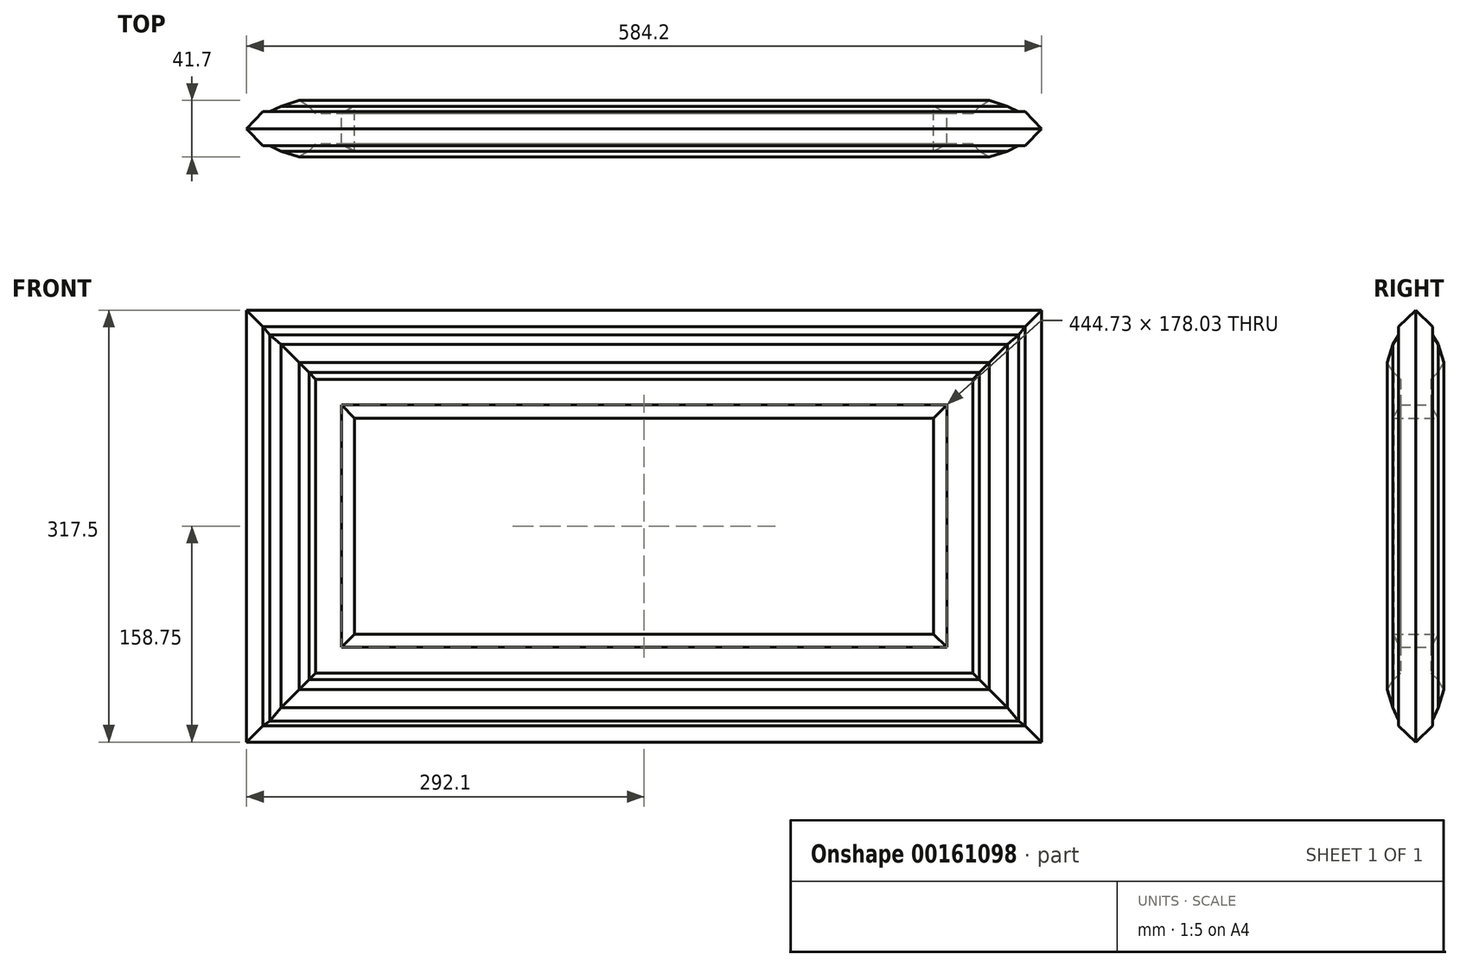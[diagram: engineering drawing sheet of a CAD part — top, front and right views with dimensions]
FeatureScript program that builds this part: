
annotation { "Feature Type Name" : "Feature", "Feature Type Description" : "" }
export const myFeature = defineFeature(function(context is Context, id is Id, definition is map)
    precondition{}
    {
        {
            var Q0;
            Q0=qCreatedBy(makeId("Front.planeOp"),FACE);
            var sketch = newSketch(context, id + "F0", { "sketchPlane" : qUnion([Q0])});
            skLineSegment(sketch, "E0.bottom", {"start": v(212.75, 79.4) * mm, "end": v(-212.75, 79.4) * mm});
            skLineSegment(sketch, "E0.top", {"start": v(212.75, -79.4) * mm, "end": v(-212.75, -79.4) * mm});
            skLineSegment(sketch, "E0.left", {"start": v(212.75, 79.4) * mm, "end": v(212.75, -79.4) * mm});
            skLineSegment(sketch, "E0.right", {"start": v(-212.75, 79.4) * mm, "end": v(-212.75, -79.4) * mm});
            skPoint(sketch, "E0.middle", {"position": v(0, 0) * mm});
            skSolve(sketch);
        }
        {
            var Q0;
            Q0 = qSketchRegion(id + "F0", true);
            extrude(context, id + "F1", {"entities" : qUnion([Q0]), "depth" : 16.67 * mm, "hasSecondDirection" : true, "secondDirectionOppositeDirection" : true, "secondDirectionDepth" : 16.67 * mm});
        }
        {
            var Q0;
            Q0=qCreatedBy(makeId("Front.planeOp"),FACE);
            var sketch = newSketch(context, id + "F2", { "sketchPlane" : qUnion([Q0])});
            skLineSegment(sketch, "E1.bottom", {"start": v(222.36, 89.01) * mm, "end": v(-222.36, 89.01) * mm});
            skLineSegment(sketch, "E1.top", {"start": v(222.36, -89.01) * mm, "end": v(-222.36, -89.01) * mm});
            skLineSegment(sketch, "E1.left", {"start": v(222.36, 89.01) * mm, "end": v(222.36, -89.01) * mm});
            skLineSegment(sketch, "E1.right", {"start": v(-222.36, 89.01) * mm, "end": v(-222.36, -89.01) * mm});
            skPoint(sketch, "E1.middle", {"position": v(0, 0) * mm});
            skLineSegment(sketch, "E2.bottom", {"start": v(241.38, 108.03) * mm, "end": v(-241.38, 108.03) * mm});
            skLineSegment(sketch, "E2.top", {"start": v(241.38, -108.03) * mm, "end": v(-241.38, -108.03) * mm});
            skLineSegment(sketch, "E2.left", {"start": v(241.38, 108.03) * mm, "end": v(241.38, -108.03) * mm});
            skLineSegment(sketch, "E2.right", {"start": v(-241.38, 108.03) * mm, "end": v(-241.38, -108.03) * mm});
            skSolve(sketch);
        }
        {
            var Q0;
            Q0 = qSketchRegion(id + "F2", true);
            extrude(context, id + "F3", {"entities" : qUnion([Q0]), "depth" : 11.13 * mm, "hasSecondDirection" : true, "secondDirectionOppositeDirection" : true, "secondDirectionDepth" : 11.13 * mm});
        }
        {
            var Q0;
            Q0=makeQuery(id+"F1.opExtrude","SWEPT_FACE",FACE,{"disambiguationData":[OSD([sQuery(id+"F0.wireOp",EDGE,"E0.right")])]});
            var Q1;
            Q1=makeQuery(id+"F3.opExtrude","SWEPT_FACE",FACE,{"disambiguationData":[OSD([sQuery(id+"F2.wireOp",EDGE,"E1.right")])]});
            loft(context, id + "F4", {"sheetProfilesArray" : [{ "sheetProfileEntities" : qUnion([Q0]) }, { "sheetProfileEntities" : qUnion([Q1]) }]});
        }
        {
            var Q0;
            Q0=makeQuery(id+"F1.opExtrude","SWEPT_FACE",FACE,{"disambiguationData":[OSD([sQuery(id+"F0.wireOp",EDGE,"E0.bottom")])]});
            var Q1;
            Q1=makeQuery(id+"F3.opExtrude","SWEPT_FACE",FACE,{"disambiguationData":[OSD([sQuery(id+"F2.wireOp",EDGE,"E1.bottom")])]});
            loft(context, id + "F5", {"sheetProfilesArray" : [{ "sheetProfileEntities" : qUnion([Q0]) }, { "sheetProfileEntities" : qUnion([Q1]) }]});
        }
        {
            var Q0;
            Q0=makeQuery(id+"F3.opExtrude","SWEPT_FACE",FACE,{"disambiguationData":[OSD([sQuery(id+"F2.wireOp",EDGE,"E1.top")])]});
            var Q1;
            Q1=makeQuery(id+"F1.opExtrude","SWEPT_FACE",FACE,{"disambiguationData":[OSD([sQuery(id+"F0.wireOp",EDGE,"E0.top")])]});
            loft(context, id + "F6", {"sheetProfilesArray" : [{ "sheetProfileEntities" : qUnion([Q0]) }, { "sheetProfileEntities" : qUnion([Q1]) }]});
        }
        {
            var Q0;
            Q0=makeQuery(id+"F1.opExtrude","SWEPT_FACE",FACE,{"disambiguationData":[OSD([sQuery(id+"F0.wireOp",EDGE,"E0.left")])]});
            var Q1;
            Q1=makeQuery(id+"F3.opExtrude","SWEPT_FACE",FACE,{"disambiguationData":[OSD([sQuery(id+"F2.wireOp",EDGE,"E1.left")])]});
            loft(context, id + "F7", {"sheetProfilesArray" : [{ "sheetProfileEntities" : qUnion([Q0]) }, { "sheetProfileEntities" : qUnion([Q1]) }]});
        }
        {
            var Q0;
            Q0=qCreatedBy(makeId("Front.planeOp"),FACE);
            var sketch = newSketch(context, id + "F8", { "sketchPlane" : qUnion([Q0])});
            skLineSegment(sketch, "E3.bottom", {"start": v(-246.18, 112.83) * mm, "end": v(246.18, 112.83) * mm});
            skLineSegment(sketch, "E3.top", {"start": v(-246.18, -112.83) * mm, "end": v(246.18, -112.83) * mm});
            skLineSegment(sketch, "E3.left", {"start": v(-246.18, 112.83) * mm, "end": v(-246.18, -112.83) * mm});
            skLineSegment(sketch, "E3.right", {"start": v(246.18, 112.83) * mm, "end": v(246.18, -112.83) * mm});
            skPoint(sketch, "E3.middle", {"position": v(0, 0) * mm});
            skSolve(sketch);
        }
        {
            var Q0;
            Q0 = qSketchRegion(id + "F8", true);
            var Q1;
            Q1 = qConstructionFilter(qBodyType(qCreatedBy(id + "F8" ,EDGE), BodyType.WIRE), ConstructionObject.NO);
            extrude(context, id + "F9", {"entities" : qUnion([Q0]), "bodyType" : ToolBodyType.SURFACE, "surfaceEntities" : qUnion([Q1]), "depth" : 16.15 * mm, "hasSecondDirection" : true, "secondDirectionOppositeDirection" : true, "secondDirectionDepth" : 16.15 * mm});
        }
        {
            var Q1;
            Q1=makeQuery(id+"F3.opExtrude","SWEPT_FACE",FACE,{"disambiguationData":[OSD([sQuery(id+"F2.wireOp",EDGE,"E2.right")])]});
            var Q2;
            Q2=makeQuery(id+"F9.opExtrude","SWEPT_FACE",FACE,{"disambiguationData":[OSD([sQuery(id+"F8.wireOp",EDGE,"E3.left")])]});
            loft(context, id + "F10", {"operationType" : NewBodyOperationType.ADD, "sheetProfilesArray" : [{ "sheetProfileEntities" : qUnion([Q1]) }, { "sheetProfileEntities" : qUnion([Q2]) }]});
        }
        {
            var Q1;
            Q1=makeQuery(id+"F9.opExtrude","SWEPT_FACE",FACE,{"disambiguationData":[OSD([sQuery(id+"F8.wireOp",EDGE,"E3.bottom")])]});
            var Q2;
            Q2=makeQuery(id+"F3.opExtrude","SWEPT_FACE",FACE,{"disambiguationData":[OSD([sQuery(id+"F2.wireOp",EDGE,"E2.bottom")])]});
            loft(context, id + "F11", {"operationType" : NewBodyOperationType.ADD, "sheetProfilesArray" : [{ "sheetProfileEntities" : qUnion([Q1]) }, { "sheetProfileEntities" : qUnion([Q2]) }]});
        }
        {
            var Q1;
            Q1=makeQuery(id+"F9.opExtrude","SWEPT_FACE",FACE,{"disambiguationData":[OSD([sQuery(id+"F8.wireOp",EDGE,"E3.right")])]});
            var Q2;
            Q2=makeQuery(id+"F3.opExtrude","SWEPT_FACE",FACE,{"disambiguationData":[OSD([sQuery(id+"F2.wireOp",EDGE,"E2.left")])]});
            loft(context, id + "F12", {"operationType" : NewBodyOperationType.ADD, "sheetProfilesArray" : [{ "sheetProfileEntities" : qUnion([Q1]) }, { "sheetProfileEntities" : qUnion([Q2]) }]});
        }
        {
            var Q1;
            Q1=makeQuery(id+"F9.opExtrude","SWEPT_FACE",FACE,{"disambiguationData":[OSD([sQuery(id+"F8.wireOp",EDGE,"E3.top")])]});
            var Q2;
            Q2=makeQuery(id+"F3.opExtrude","SWEPT_FACE",FACE,{"disambiguationData":[OSD([sQuery(id+"F2.wireOp",EDGE,"E2.top")])]});
            loft(context, id + "F13", {"operationType" : NewBodyOperationType.ADD, "sheetProfilesArray" : [{ "sheetProfileEntities" : qUnion([Q1]) }, { "sheetProfileEntities" : qUnion([Q2]) }]});
        }
        {
            var Q0;
            Q0=qCreatedBy(makeId("Front.planeOp"),FACE);
            var sketch = newSketch(context, id + "F14", { "sketchPlane" : qUnion([Q0])});
            skLineSegment(sketch, "E4.bottom", {"start": v(253.5, 120.14) * mm, "end": v(-253.5, 120.14) * mm});
            skLineSegment(sketch, "E4.top", {"start": v(253.5, -120.14) * mm, "end": v(-253.5, -120.14) * mm});
            skLineSegment(sketch, "E4.left", {"start": v(253.5, 120.14) * mm, "end": v(253.5, -120.14) * mm});
            skLineSegment(sketch, "E4.right", {"start": v(-253.5, 120.14) * mm, "end": v(-253.5, -120.14) * mm});
            skPoint(sketch, "E4.middle", {"position": v(0, 0) * mm});
            skSolve(sketch);
        }
        {
            var Q0;
            Q0 = qConstructionFilter(qBodyType(qCreatedBy(id + "F14" ,EDGE), BodyType.WIRE), ConstructionObject.NO);
            extrude(context, id + "F15", {"bodyType" : ToolBodyType.SURFACE, "surfaceEntities" : qUnion([Q0]), "depth" : 20.85 * mm, "hasSecondDirection" : true, "secondDirectionOppositeDirection" : true, "secondDirectionDepth" : 20.85 * mm});
        }
        {
            var Q1;
            Q1=makeQuery(id+"F9.opExtrude","SWEPT_FACE",FACE,{"disambiguationData":[OSD([sQuery(id+"F8.wireOp",EDGE,"E3.bottom")])]});
            var Q2;
            Q2=makeQuery(id+"F15.opExtrude","SWEPT_FACE",FACE,{"disambiguationData":[OSD([sQuery(id+"F14.wireOp",EDGE,"E4.bottom")])]});
            loft(context, id + "F16", {"operationType" : NewBodyOperationType.ADD, "sheetProfilesArray" : [{ "sheetProfileEntities" : qUnion([Q1]) }, { "sheetProfileEntities" : qUnion([Q2]) }]});
        }
        {
            var Q1;
            Q1=makeQuery(id+"F15.opExtrude","SWEPT_FACE",FACE,{"disambiguationData":[OSD([sQuery(id+"F14.wireOp",EDGE,"E4.right")])]});
            var Q2;
            Q2=makeQuery(id+"F9.opExtrude","SWEPT_FACE",FACE,{"disambiguationData":[OSD([sQuery(id+"F8.wireOp",EDGE,"E3.left")])]});
            loft(context, id + "F17", {"operationType" : NewBodyOperationType.ADD, "sheetProfilesArray" : [{ "sheetProfileEntities" : qUnion([Q1]) }, { "sheetProfileEntities" : qUnion([Q2]) }]});
        }
        {
            var Q1;
            Q1=makeQuery(id+"F15.opExtrude","SWEPT_FACE",FACE,{"disambiguationData":[OSD([sQuery(id+"F14.wireOp",EDGE,"E4.top")])]});
            var Q2;
            Q2=makeQuery(id+"F9.opExtrude","SWEPT_FACE",FACE,{"disambiguationData":[OSD([sQuery(id+"F8.wireOp",EDGE,"E3.top")])]});
            loft(context, id + "F18", {"operationType" : NewBodyOperationType.ADD, "sheetProfilesArray" : [{ "sheetProfileEntities" : qUnion([Q1]) }, { "sheetProfileEntities" : qUnion([Q2]) }]});
        }
        {
            var Q1;
            Q1=makeQuery(id+"F15.opExtrude","SWEPT_FACE",FACE,{"disambiguationData":[OSD([sQuery(id+"F14.wireOp",EDGE,"E4.left")])]});
            var Q2;
            Q2=makeQuery(id+"F9.opExtrude","SWEPT_FACE",FACE,{"disambiguationData":[OSD([sQuery(id+"F8.wireOp",EDGE,"E3.right")])]});
            loft(context, id + "F19", {"operationType" : NewBodyOperationType.ADD, "sheetProfilesArray" : [{ "sheetProfileEntities" : qUnion([Q1]) }, { "sheetProfileEntities" : qUnion([Q2]) }]});
        }
        {
            var Q0;
            Q0=qCreatedBy(makeId("Front.planeOp"),FACE);
            var sketch = newSketch(context, id + "F20", { "sketchPlane" : qUnion([Q0])});
            skLineSegment(sketch, "E5.bottom", {"start": v(-266.87, -133.52) * mm, "end": v(266.87, -133.52) * mm});
            skLineSegment(sketch, "E5.top", {"start": v(-266.87, 133.52) * mm, "end": v(266.87, 133.52) * mm});
            skLineSegment(sketch, "E5.left", {"start": v(-266.87, -133.52) * mm, "end": v(-266.87, 133.52) * mm});
            skLineSegment(sketch, "E5.right", {"start": v(266.87, -133.52) * mm, "end": v(266.87, 133.52) * mm});
            skPoint(sketch, "E5.middle", {"position": v(0, 0) * mm});
            skSolve(sketch);
        }
        {
            var Q0;
            Q0 = qSketchRegion(id + "F20", true);
            var Q1;
            Q1 = qConstructionFilter(qBodyType(qCreatedBy(id + "F20" ,EDGE), BodyType.WIRE), ConstructionObject.NO);
            extrude(context, id + "F21", {"entities" : qUnion([Q0]), "bodyType" : ToolBodyType.SURFACE, "surfaceEntities" : qUnion([Q1]), "depth" : 16.59 * mm, "hasSecondDirection" : true, "secondDirectionOppositeDirection" : true, "secondDirectionDepth" : 16.59 * mm});
        }
        {
            var Q1;
            Q1=makeQuery(id+"F15.opExtrude","SWEPT_FACE",FACE,{"disambiguationData":[OSD([sQuery(id+"F14.wireOp",EDGE,"E4.right")])]});
            var Q2;
            Q2=makeQuery(id+"F21.opExtrude","SWEPT_FACE",FACE,{"disambiguationData":[OSD([sQuery(id+"F20.wireOp",EDGE,"E5.left")])]});
            loft(context, id + "F22", {"operationType" : NewBodyOperationType.ADD, "sheetProfilesArray" : [{ "sheetProfileEntities" : qUnion([Q1]) }, { "sheetProfileEntities" : qUnion([Q2]) }]});
        }
        {
            var Q1;
            Q1=makeQuery(id+"F21.opExtrude","SWEPT_FACE",FACE,{"disambiguationData":[OSD([sQuery(id+"F20.wireOp",EDGE,"E5.bottom")])]});
            var Q2;
            Q2=makeQuery(id+"F15.opExtrude","SWEPT_FACE",FACE,{"disambiguationData":[OSD([sQuery(id+"F14.wireOp",EDGE,"E4.top")])]});
            loft(context, id + "F23", {"operationType" : NewBodyOperationType.ADD, "sheetProfilesArray" : [{ "sheetProfileEntities" : qUnion([Q1]) }, { "sheetProfileEntities" : qUnion([Q2]) }]});
        }
        {
            var Q1;
            Q1=makeQuery(id+"F21.opExtrude","SWEPT_FACE",FACE,{"disambiguationData":[OSD([sQuery(id+"F20.wireOp",EDGE,"E5.top")])]});
            var Q2;
            Q2=makeQuery(id+"F15.opExtrude","SWEPT_FACE",FACE,{"disambiguationData":[OSD([sQuery(id+"F14.wireOp",EDGE,"E4.bottom")])]});
            loft(context, id + "F24", {"operationType" : NewBodyOperationType.ADD, "sheetProfilesArray" : [{ "sheetProfileEntities" : qUnion([Q1]) }, { "sheetProfileEntities" : qUnion([Q2]) }]});
        }
        {
            var Q1;
            Q1=makeQuery(id+"F21.opExtrude","SWEPT_FACE",FACE,{"disambiguationData":[OSD([sQuery(id+"F20.wireOp",EDGE,"E5.right")])]});
            var Q2;
            Q2=makeQuery(id+"F15.opExtrude","SWEPT_FACE",FACE,{"disambiguationData":[OSD([sQuery(id+"F14.wireOp",EDGE,"E4.left")])]});
            loft(context, id + "F25", {"operationType" : NewBodyOperationType.ADD, "sheetProfilesArray" : [{ "sheetProfileEntities" : qUnion([Q1]) }, { "sheetProfileEntities" : qUnion([Q2]) }]});
        }
        {
            var Q0;
            Q0=qCreatedBy(makeId("Front.planeOp"),FACE);
            var sketch = newSketch(context, id + "F26", { "sketchPlane" : qUnion([Q0])});
            skLineSegment(sketch, "E6.bottom", {"start": v(275.22, 140.61) * mm, "end": v(-275.22, 140.61) * mm});
            skLineSegment(sketch, "E6.top", {"start": v(275.22, -143.13) * mm, "end": v(-275.22, -143.13) * mm});
            skLineSegment(sketch, "E6.left", {"start": v(275.22, 140.61) * mm, "end": v(275.22, -143.13) * mm});
            skLineSegment(sketch, "E6.right", {"start": v(-275.22, 140.61) * mm, "end": v(-275.22, -143.13) * mm});
            skPoint(sketch, "E6.middle", {"position": v(0, -1.26) * mm});
            skSolve(sketch);
        }
        {
            var Q0;
            Q0 = qSketchRegion(id + "F26", true);
            var Q1;
            Q1 = qConstructionFilter(qBodyType(qCreatedBy(id + "F26" ,EDGE), BodyType.WIRE), ConstructionObject.NO);
            extrude(context, id + "F27", {"entities" : qUnion([Q0]), "bodyType" : ToolBodyType.SURFACE, "surfaceEntities" : qUnion([Q1]), "depth" : 12.34 * mm, "hasSecondDirection" : true, "secondDirectionOppositeDirection" : true, "secondDirectionDepth" : 12.34 * mm});
        }
        {
            var Q1;
            Q1=makeQuery(id+"F21.opExtrude","SWEPT_FACE",FACE,{"disambiguationData":[OSD([sQuery(id+"F20.wireOp",EDGE,"E5.left")])]});
            var Q2;
            Q2=makeQuery(id+"F27.opExtrude","SWEPT_FACE",FACE,{"disambiguationData":[OSD([sQuery(id+"F26.wireOp",EDGE,"E6.right")])]});
            loft(context, id + "F28", {"operationType" : NewBodyOperationType.ADD, "sheetProfilesArray" : [{ "sheetProfileEntities" : qUnion([Q1]) }, { "sheetProfileEntities" : qUnion([Q2]) }]});
        }
        {
            var Q1;
            Q1=makeQuery(id+"F21.opExtrude","SWEPT_FACE",FACE,{"disambiguationData":[OSD([sQuery(id+"F20.wireOp",EDGE,"E5.top")])]});
            var Q2;
            Q2=makeQuery(id+"F27.opExtrude","SWEPT_FACE",FACE,{"disambiguationData":[OSD([sQuery(id+"F26.wireOp",EDGE,"E6.bottom")])]});
            loft(context, id + "F29", {"operationType" : NewBodyOperationType.ADD, "sheetProfilesArray" : [{ "sheetProfileEntities" : qUnion([Q1]) }, { "sheetProfileEntities" : qUnion([Q2]) }]});
        }
        {
            var Q1;
            Q1=makeQuery(id+"F27.opExtrude","SWEPT_FACE",FACE,{"disambiguationData":[OSD([sQuery(id+"F26.wireOp",EDGE,"E6.top")])]});
            var Q2;
            Q2=makeQuery(id+"F21.opExtrude","SWEPT_FACE",FACE,{"disambiguationData":[OSD([sQuery(id+"F20.wireOp",EDGE,"E5.bottom")])]});
            loft(context, id + "F30", {"operationType" : NewBodyOperationType.ADD, "sheetProfilesArray" : [{ "sheetProfileEntities" : qUnion([Q1]) }, { "sheetProfileEntities" : qUnion([Q2]) }]});
        }
        {
            var Q1;
            Q1=makeQuery(id+"F27.opExtrude","SWEPT_FACE",FACE,{"disambiguationData":[OSD([sQuery(id+"F26.wireOp",EDGE,"E6.left")])]});
            var Q2;
            Q2=makeQuery(id+"F21.opExtrude","SWEPT_FACE",FACE,{"disambiguationData":[OSD([sQuery(id+"F20.wireOp",EDGE,"E5.right")])]});
            loft(context, id + "F31", {"operationType" : NewBodyOperationType.ADD, "sheetProfilesArray" : [{ "sheetProfileEntities" : qUnion([Q1]) }, { "sheetProfileEntities" : qUnion([Q2]) }]});
        }
        {
            var Q0;
            Q0=qCreatedBy(makeId("Front.planeOp"),FACE);
            var sketch = newSketch(context, id + "F32", { "sketchPlane" : qUnion([Q0])});
            skLineSegment(sketch, "E7.bottom", {"start": v(-280.02, -146.67) * mm, "end": v(280.02, -146.67) * mm});
            skLineSegment(sketch, "E7.top", {"start": v(-280.02, 146.67) * mm, "end": v(280.02, 146.67) * mm});
            skLineSegment(sketch, "E7.left", {"start": v(-280.02, -146.67) * mm, "end": v(-280.02, 146.67) * mm});
            skLineSegment(sketch, "E7.right", {"start": v(280.02, -146.67) * mm, "end": v(280.02, 146.67) * mm});
            skPoint(sketch, "E7.middle", {"position": v(0, 0) * mm});
            skSolve(sketch);
        }
        {
            var Q0;
            Q0 = qSketchRegion(id + "F32", true);
            var Q1;
            Q1 = qConstructionFilter(qBodyType(qCreatedBy(id + "F32" ,EDGE), BodyType.WIRE), ConstructionObject.NO);
            extrude(context, id + "F33", {"entities" : qUnion([Q0]), "bodyType" : ToolBodyType.SURFACE, "surfaceEntities" : qUnion([Q1]), "depth" : 12.5 * mm, "hasSecondDirection" : true, "secondDirectionOppositeDirection" : true, "secondDirectionDepth" : 12.5 * mm});
        }
        {
            var Q1;
            Q1=makeQuery(id+"F33.opExtrude","SWEPT_FACE",FACE,{"disambiguationData":[OSD([sQuery(id+"F32.wireOp",EDGE,"E7.left")])]});
            var Q2;
            Q2=makeQuery(id+"F27.opExtrude","SWEPT_FACE",FACE,{"disambiguationData":[OSD([sQuery(id+"F26.wireOp",EDGE,"E6.right")])]});
            loft(context, id + "F34", {"operationType" : NewBodyOperationType.ADD, "sheetProfilesArray" : [{ "sheetProfileEntities" : qUnion([Q1]) }, { "sheetProfileEntities" : qUnion([Q2]) }]});
        }
        {
            var Q1;
            Q1=makeQuery(id+"F33.opExtrude","SWEPT_FACE",FACE,{"disambiguationData":[OSD([sQuery(id+"F32.wireOp",EDGE,"E7.top")])]});
            var Q2;
            Q2=makeQuery(id+"F27.opExtrude","SWEPT_FACE",FACE,{"disambiguationData":[OSD([sQuery(id+"F26.wireOp",EDGE,"E6.bottom")])]});
            loft(context, id + "F35", {"operationType" : NewBodyOperationType.ADD, "sheetProfilesArray" : [{ "sheetProfileEntities" : qUnion([Q1]) }, { "sheetProfileEntities" : qUnion([Q2]) }]});
        }
        {
            var Q1;
            Q1=makeQuery(id+"F33.opExtrude","SWEPT_FACE",FACE,{"disambiguationData":[OSD([sQuery(id+"F32.wireOp",EDGE,"E7.bottom")])]});
            var Q2;
            Q2=makeQuery(id+"F27.opExtrude","SWEPT_FACE",FACE,{"disambiguationData":[OSD([sQuery(id+"F26.wireOp",EDGE,"E6.top")])]});
            loft(context, id + "F36", {"operationType" : NewBodyOperationType.ADD, "sheetProfilesArray" : [{ "sheetProfileEntities" : qUnion([Q1]) }, { "sheetProfileEntities" : qUnion([Q2]) }]});
        }
        {
            var Q1;
            Q1=makeQuery(id+"F33.opExtrude","SWEPT_FACE",FACE,{"disambiguationData":[OSD([sQuery(id+"F32.wireOp",EDGE,"E7.right")])]});
            var Q2;
            Q2=makeQuery(id+"F27.opExtrude","SWEPT_FACE",FACE,{"disambiguationData":[OSD([sQuery(id+"F26.wireOp",EDGE,"E6.left")])]});
            loft(context, id + "F37", {"operationType" : NewBodyOperationType.ADD, "sheetProfilesArray" : [{ "sheetProfileEntities" : qUnion([Q1]) }, { "sheetProfileEntities" : qUnion([Q2]) }]});
        }
        {
            var Q0;
            Q0=qCreatedBy(makeId("Front.planeOp"),FACE);
            var sketch = newSketch(context, id + "F38", { "sketchPlane" : qUnion([Q0])});
            skLineSegment(sketch, "E8.bottom", {"start": v(-292.1, -158.75) * mm, "end": v(292.1, -158.75) * mm});
            skLineSegment(sketch, "E8.top", {"start": v(-292.1, 158.75) * mm, "end": v(292.1, 158.75) * mm});
            skLineSegment(sketch, "E8.left", {"start": v(-292.1, -158.75) * mm, "end": v(-292.1, 158.75) * mm});
            skLineSegment(sketch, "E8.right", {"start": v(292.1, -158.75) * mm, "end": v(292.1, 158.75) * mm});
            skPoint(sketch, "E8.middle", {"position": v(0, 0) * mm});
            skSolve(sketch);
        }
        {
            var Q0;
            Q0 = qSketchRegion(id + "F38", true);
            var Q1;
            Q1 = qConstructionFilter(qBodyType(qCreatedBy(id + "F38" ,EDGE), BodyType.WIRE), ConstructionObject.NO);
            extrude(context, id + "F39", {"entities" : qUnion([Q0]), "bodyType" : ToolBodyType.SURFACE, "surfaceEntities" : qUnion([Q1]), "depth" : 1.75 / 50.8 * mm, "hasSecondDirection" : true, "secondDirectionOppositeDirection" : true, "secondDirectionDepth" : 1.75 / 50.8 * mm});
        }
        {
            var Q1;
            Q1=makeQuery(id+"F39.opExtrude","SWEPT_FACE",FACE,{"disambiguationData":[OSD([sQuery(id+"F38.wireOp",EDGE,"E8.left")])]});
            var Q2;
            Q2=makeQuery(id+"F33.opExtrude","SWEPT_FACE",FACE,{"disambiguationData":[OSD([sQuery(id+"F32.wireOp",EDGE,"E7.left")])]});
            loft(context, id + "F40", {"operationType" : NewBodyOperationType.ADD, "sheetProfilesArray" : [{ "sheetProfileEntities" : qUnion([Q1]) }, { "sheetProfileEntities" : qUnion([Q2]) }]});
        }
        {
            var Q1;
            Q1=makeQuery(id+"F33.opExtrude","SWEPT_FACE",FACE,{"disambiguationData":[OSD([sQuery(id+"F32.wireOp",EDGE,"E7.top")])]});
            var Q2;
            Q2=makeQuery(id+"F39.opExtrude","SWEPT_FACE",FACE,{"disambiguationData":[OSD([sQuery(id+"F38.wireOp",EDGE,"E8.top")])]});
            loft(context, id + "F41", {"operationType" : NewBodyOperationType.ADD, "sheetProfilesArray" : [{ "sheetProfileEntities" : qUnion([Q1]) }, { "sheetProfileEntities" : qUnion([Q2]) }]});
        }
        {
            var Q1;
            Q1=makeQuery(id+"F39.opExtrude","SWEPT_FACE",FACE,{"disambiguationData":[OSD([sQuery(id+"F38.wireOp",EDGE,"E8.right")])]});
            var Q2;
            Q2=makeQuery(id+"F33.opExtrude","SWEPT_FACE",FACE,{"disambiguationData":[OSD([sQuery(id+"F32.wireOp",EDGE,"E7.right")])]});
            loft(context, id + "F42", {"operationType" : NewBodyOperationType.ADD, "sheetProfilesArray" : [{ "sheetProfileEntities" : qUnion([Q1]) }, { "sheetProfileEntities" : qUnion([Q2]) }]});
        }
        {
            var Q1;
            Q1=makeQuery(id+"F39.opExtrude","SWEPT_FACE",FACE,{"disambiguationData":[OSD([sQuery(id+"F38.wireOp",EDGE,"E8.bottom")])]});
            var Q2;
            Q2=makeQuery(id+"F33.opExtrude","SWEPT_FACE",FACE,{"disambiguationData":[OSD([sQuery(id+"F32.wireOp",EDGE,"E7.bottom")])]});
            loft(context, id + "F43", {"operationType" : NewBodyOperationType.ADD, "sheetProfilesArray" : [{ "sheetProfileEntities" : qUnion([Q1]) }, { "sheetProfileEntities" : qUnion([Q2]) }]});
        }
    });
